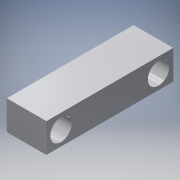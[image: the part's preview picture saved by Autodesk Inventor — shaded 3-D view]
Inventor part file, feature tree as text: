
AUTODESK INVENTOR PART (.ipt)
format: ipt  version: 2016 (Build 200138000, 138)  size: 125,440 bytes
history: native  units: mm
features: sketch x4, extrude x3, hole x1
ambient origin geometry x8: Origin, YZ Plane, XZ Plane, XY Plane, X Axis, Y Axis, Z Axis, Center Point
bodies: Solid1 (feature_tree)
feature tree (8):
  extrude  "Extrusion1"  Depth=20.3mm
  sketch  "Sketch2"  dims[d2=65.0mm d3=0.0mm d4=6.5mm]
  extrude  "Extrusion2"  Depth=65.0mm
  extrude  "Extrusion3"  Depth=11.0mm
  hole  "Hole1"  [1 undecoded]
  sketch  "Sketch4"  dims[d9=11.0mm d10=50.0mm d11=0.0mm d12=21.3mm d13=0.0mm d14=6.0mm d15=4.917mm d16=15.0mm d17=4.0mm d18=2.0mm d19=90.0deg d20=15.1mm d21=20.594885mm d22=16.395mm d23=6.0mm d24=25.0mm d26=25.0mm d27=25.0mm]
  sketch  "Sketch1"  dims[d0=15.0mm d1=20.3mm]
  sketch  "Sketch3"  dims[d5=6.5mm d8=11.0mm]
note: 1 required parameter value undecoded (feature->parameter linkage not recoverable at this tier; creation-order binding heuristic only, values carry confidence <= 0.55)
